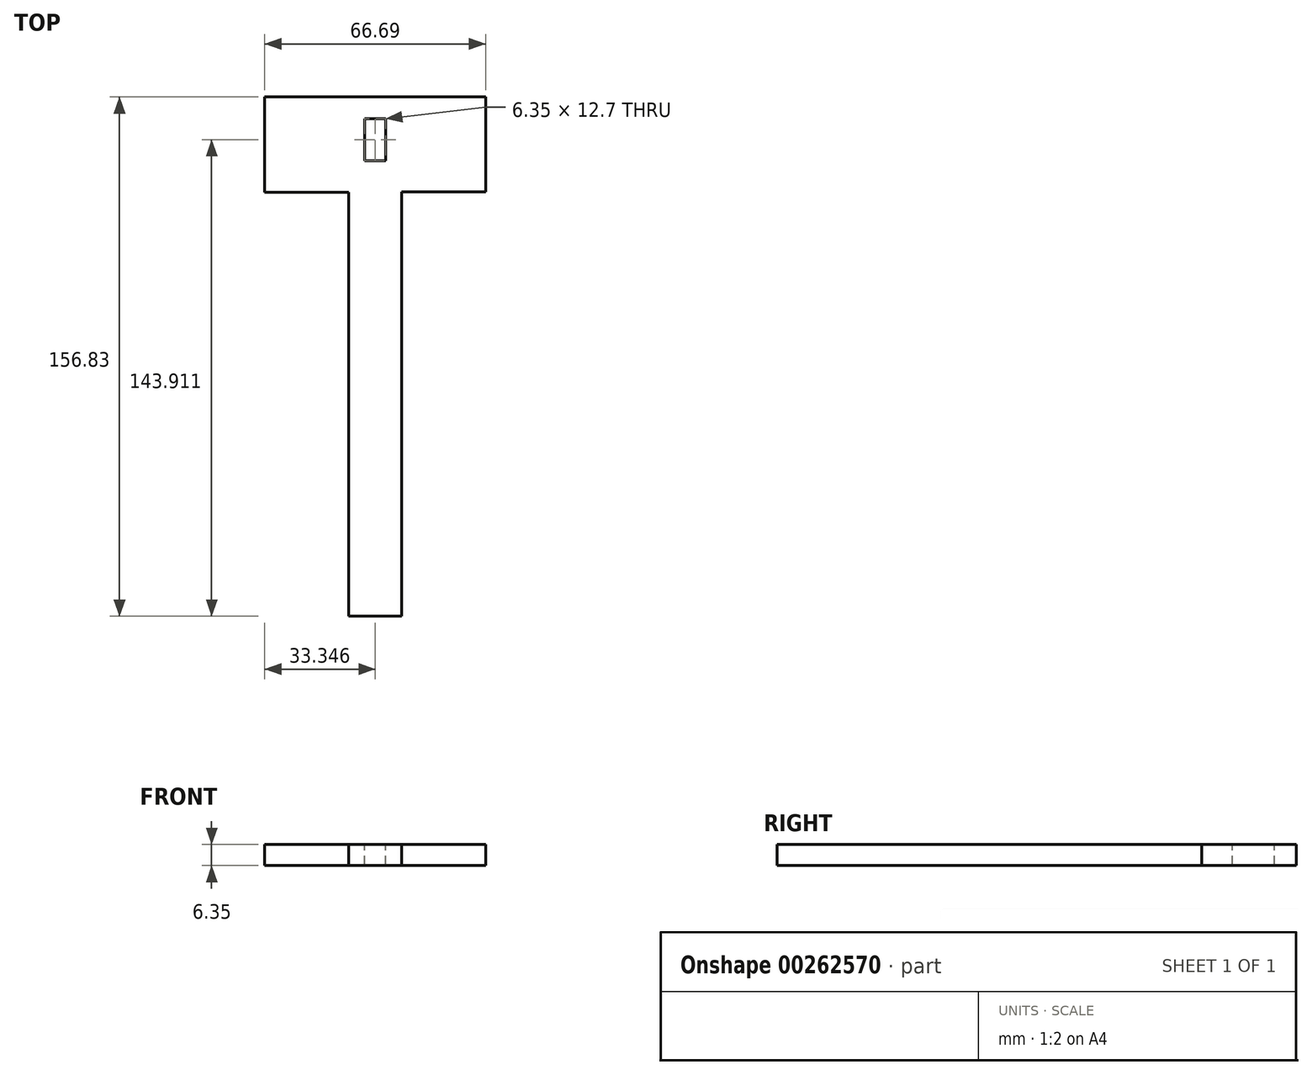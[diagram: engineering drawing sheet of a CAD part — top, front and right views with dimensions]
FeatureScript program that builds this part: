
annotation { "Feature Type Name" : "Feature", "Feature Type Description" : "" }
export const myFeature = defineFeature(function(context is Context, id is Id, definition is map)
    precondition{}
    {
        {
            var Q0;
            Q0=qCreatedBy(makeId("Top.planeOp"),FACE);
            var sketch = newSketch(context, id + "F0", { "sketchPlane" : qUnion([Q0])});
            skLineSegment(sketch, "E0.bottom", {"start": v(0, 0) * mm, "end": v(15.9, 0) * mm});
            skLineSegment(sketch, "E0.top", {"start": v(0, 118.73) * mm, "end": v(15.9, 118.73) * mm});
            skLineSegment(sketch, "E0.left", {"start": v(0, 0) * mm, "end": v(0, 118.73) * mm});
            skLineSegment(sketch, "E0.right", {"start": v(15.9, 0) * mm, "end": v(15.9, 118.73) * mm});
            skSolve(sketch);
        }
        {
            var Q0;
            Q0 = qSketchRegion(id + "F0", true);
            extrude(context, id + "F1", {"entities" : qUnion([Q0]), "depth" : 5.08 * mm});
        }
        {
            var Q0;
            Q0=makeQuery(id+"F1.opExtrude","SWEPT_FACE",FACE,{"disambiguationData":[OSD([sQuery(id+"F0.wireOp",EDGE,"E0.right")])]});
            var sketch = newSketch(context, id + "F2", { "sketchPlane" : qUnion([Q0])});
            skLineSegment(sketch, "E1.bottom", {"start": v(118.73, 5.08) * mm, "end": v(102.78, 5.08) * mm});
            skLineSegment(sketch, "E1.top", {"start": v(118.73, 0) * mm, "end": v(102.78, 0) * mm});
            skLineSegment(sketch, "E1.left", {"start": v(118.73, 5.08) * mm, "end": v(118.73, 0) * mm});
            skLineSegment(sketch, "E1.right", {"start": v(102.78, 5.08) * mm, "end": v(102.78, 0) * mm});
            skSolve(sketch);
        }
        {
            var Q0;
            Q0=makeQuery(id+"F2.imprint","IMPRINT",FACE,{"disambiguationData":[TD([[makeQuery(id+"F2.imprint","IMPRINT",EDGE,{"derivedFrom":sQuery(id+"F2.wireOp",EDGE,"E1.bottom")}),-1.0]])]});
            extrude(context, id + "F3", {"entities" : qUnion([Q0]), "operationType" : NewBodyOperationType.ADD, "depth" : 25.4 * mm});
        }
        {
            var Q0;
            Q0=makeQuery(id+"F1.opExtrude","SWEPT_FACE",FACE,{"disambiguationData":[OSD([sQuery(id+"F0.wireOp",EDGE,"E0.left")])]});
            var sketch = newSketch(context, id + "F4", { "sketchPlane" : qUnion([Q0])});
            skLineSegment(sketch, "E2.bottom", {"start": v(-118.73, 5.08) * mm, "end": v(-102.67, 5.08) * mm});
            skLineSegment(sketch, "E2.top", {"start": v(-118.73, 0) * mm, "end": v(-102.67, 0) * mm});
            skLineSegment(sketch, "E2.left", {"start": v(-118.73, 5.08) * mm, "end": v(-118.73, 0) * mm});
            skLineSegment(sketch, "E2.right", {"start": v(-102.67, 5.08) * mm, "end": v(-102.67, 0) * mm});
            skSolve(sketch);
        }
        {
            var Q0;
            Q0=makeQuery(id+"F4.imprint","IMPRINT",FACE,{"disambiguationData":[TD([[makeQuery(id+"F4.imprint","IMPRINT",EDGE,{"derivedFrom":sQuery(id+"F4.wireOp",EDGE,"E2.bottom")}),1.0]])]});
            extrude(context, id + "F5", {"entities" : qUnion([Q0]), "operationType" : NewBodyOperationType.ADD, "depth" : 25.4 * mm});
        }
        {
            var Q0;
            Q0=makeQuery(id+"F5.boolean.opBoolean","MERGE",FACE,{"derivedFrom":[makeQuery(id+"F3.boolean.opBoolean","MERGE",FACE,{"derivedFrom":[makeQuery(id+"F1.opExtrude","SWEPT_FACE",FACE,{"disambiguationData":[OSD([sQuery(id+"F0.wireOp",EDGE,"E0.top")])]}),makeQuery(id+"F3.opExtrude","SWEPT_FACE",FACE,{"disambiguationData":[OSD([sQuery(id+"F2.wireOp",EDGE,"E1.left")])]})]}),makeQuery(id+"F5.opExtrude","SWEPT_FACE",FACE,{"disambiguationData":[OSD([sQuery(id+"F4.wireOp",EDGE,"E2.left")])]})]});
            extrude(context, id + "F6", {"entities" : qUnion([Q0]), "operationType" : NewBodyOperationType.ADD, "depth" : 12.7 * mm});
        }
        {
            var Q0;
            Q0=makeQuery(id+"F1.opExtrude","SWEPT_FACE",FACE,{"disambiguationData":[OSD([sQuery(id+"F0.wireOp",EDGE,"E0.bottom")])]});
            extrude(context, id + "F7", {"entities" : qUnion([Q0]), "operationType" : NewBodyOperationType.ADD, "depth" : 25.4 * mm});
        }
        {
            var Q0;
            {var subQ0=sQuery(id+"F0.wireOp",EDGE,"E0.bottom");var subQ1=sQuery(id+"F4.wireOp",EDGE,"E2.bottom");var subQ2=sQuery(id+"F2.wireOp",EDGE,"E1.bottom");var subQ3=sQuery(id+"F0.wireOp",EDGE,"E0.top");Q0=makeQuery(id+"F7.boolean.opBoolean","MERGE",FACE,{"derivedFrom":[makeQuery(id+"F6.boolean.opBoolean","MERGE",FACE,{"derivedFrom":[makeQuery(id+"F5.boolean.opBoolean","MERGE",FACE,{"derivedFrom":[makeQuery(id+"F3.boolean.opBoolean","MERGE",FACE,{"derivedFrom":[makeQuery(id+"F1.opExtrude","CAP_FACE",FACE,{"disambiguationData":[OSD([subQ0,subQ3,sQuery(id+"F0.wireOp",EDGE,"E0.left"),sQuery(id+"F0.wireOp",EDGE,"E0.right")])],"isStart":false}),makeQuery(id+"F3.opExtrude","SWEPT_FACE",FACE,{"disambiguationData":[OSD([subQ2])]})]}),makeQuery(id+"F5.opExtrude","SWEPT_FACE",FACE,{"disambiguationData":[OSD([subQ1])]})]}),makeQuery(id+"F6.opExtrude","SWEPT_FACE",FACE,{"disambiguationData":[OSD([subQ3,subQ2,sQuery(id+"F2.wireOp",EDGE,"E1.left"),subQ1,sQuery(id+"F4.wireOp",EDGE,"E2.left")])]})]}),makeQuery(id+"F7.opExtrude","SWEPT_FACE",FACE,{"disambiguationData":[OSD([subQ0]),TDD([makeQuery(id+"F1.opExtrude","CAP_EDGE",EDGE,{"disambiguationData":[OSD([subQ0])],"isStart":false})])]})]});}
            var sketch = newSketch(context, id + "F8", { "sketchPlane" : qUnion([Q0])});
            skLineSegment(sketch, "E3.bottom", {"start": v(4.77, 112.16) * mm, "end": v(11.12, 112.16) * mm});
            skLineSegment(sketch, "E3.top", {"start": v(4.77, 124.86) * mm, "end": v(11.12, 124.86) * mm});
            skLineSegment(sketch, "E3.left", {"start": v(4.77, 112.16) * mm, "end": v(4.77, 124.86) * mm});
            skLineSegment(sketch, "E3.right", {"start": v(11.12, 112.16) * mm, "end": v(11.12, 124.86) * mm});
            skPoint(sketch, "E3.middle", {"position": v(7.95, 118.51) * mm});
            skPoint(sketch, "E3.middle.positionSnap0", {"position": v(7.95, 131.43) * mm});
            skPoint(sketch, "E3.centerSnap0", {"position": v(7.95, 131.43) * mm});
            skSolve(sketch);
        }
        {
            var Q0;
            Q0=makeQuery(id+"F8.imprint","IMPRINT",FACE,{"disambiguationData":[TD([[makeQuery(id+"F8.imprint","IMPRINT",EDGE,{"derivedFrom":sQuery(id+"F8.wireOp",EDGE,"E3.bottom")}),1.0]])]});
            extrude(context, id + "F9", {"entities" : qUnion([Q0]), "operationType" : NewBodyOperationType.REMOVE, "oppositeDirection" : true, "depth" : 25.4 * mm});
        }
        {
            var Q0;
            {var subQ0=sQuery(id+"F0.wireOp",EDGE,"E0.bottom");var subQ1=sQuery(id+"F4.wireOp",EDGE,"E2.bottom");var subQ2=sQuery(id+"F2.wireOp",EDGE,"E1.bottom");var subQ3=sQuery(id+"F0.wireOp",EDGE,"E0.top");Q0=makeQuery(id+"F7.boolean.opBoolean","MERGE",FACE,{"derivedFrom":[makeQuery(id+"F6.boolean.opBoolean","MERGE",FACE,{"derivedFrom":[makeQuery(id+"F5.boolean.opBoolean","MERGE",FACE,{"derivedFrom":[makeQuery(id+"F3.boolean.opBoolean","MERGE",FACE,{"derivedFrom":[makeQuery(id+"F1.opExtrude","CAP_FACE",FACE,{"disambiguationData":[OSD([subQ0,subQ3,sQuery(id+"F0.wireOp",EDGE,"E0.left"),sQuery(id+"F0.wireOp",EDGE,"E0.right")])],"isStart":false}),makeQuery(id+"F3.opExtrude","SWEPT_FACE",FACE,{"disambiguationData":[OSD([subQ2])]})]}),makeQuery(id+"F5.opExtrude","SWEPT_FACE",FACE,{"disambiguationData":[OSD([subQ1])]})]}),makeQuery(id+"F6.opExtrude","SWEPT_FACE",FACE,{"disambiguationData":[OSD([subQ3,subQ2,sQuery(id+"F2.wireOp",EDGE,"E1.left"),subQ1,sQuery(id+"F4.wireOp",EDGE,"E2.left")])]})]}),makeQuery(id+"F7.opExtrude","SWEPT_FACE",FACE,{"disambiguationData":[OSD([subQ0]),TDD([makeQuery(id+"F1.opExtrude","CAP_EDGE",EDGE,{"disambiguationData":[OSD([subQ0])],"isStart":false})])]})]});}
            extrude(context, id + "F10", {"entities" : qUnion([Q0]), "operationType" : NewBodyOperationType.ADD, "depth" : 1.27 * mm});
        }
    });
